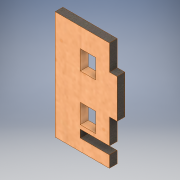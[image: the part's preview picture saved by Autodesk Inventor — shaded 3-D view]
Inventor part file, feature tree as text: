
AUTODESK INVENTOR PART (.ipt)
format: ipt  version: 2019 (Build 230136000, 136)  size: 142,848 bytes
history: native  units: mm
features: other x1, extrude x1, sketch x1
ambient origin geometry x8: Origin, YZ Plane, XZ Plane, XY Plane, X Axis, Y Axis, Z Axis, Center Point
bodies: Body1 (feature_tree)
feature tree (3):
  other  "Твердое тело1"
  extrude  "Выдавливание1"  Depth=4.0mm
  sketch  "Эскиз1"
